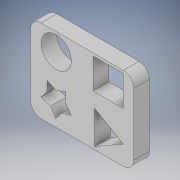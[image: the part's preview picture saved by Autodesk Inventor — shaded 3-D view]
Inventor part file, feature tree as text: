
AUTODESK INVENTOR PART (.ipt)
format: ipt  version: 2017 (Build 210142000, 142)  size: 197,120 bytes
history: native  units: in
note: dims shown in document units (in); Inventor stores cm internally (conversion verified against a paired STEP export)
features: extrude x2, shell x1, sketch x1, projected_geometry x1
ambient origin geometry x8: Origin, YZ Plane, XZ Plane, XY Plane, X Axis, Y Axis, Z Axis, Center Point
bodies: Solid1 (feature_tree)
feature tree (5):
  extrude  "Extrusion1"  Depth=1.59in
  extrude  "Extrusion2"  Depth=0.2in
  shell  "Shell1"  Thickness=0.3in
  sketch  "Sketch1"  dims[d0=1.975in d1=1.59in d2=0.2in d3=0.3in d4=0.0in d10=0.58in d11=0.05in d12=0.2in d13=0.58in d14=0.58in d15=0.58in d16=0.2in d17=0.05in d18=0.638in d19=0.2in d20=0.05in d21=0.605in d23=0.187in d25=0.187in d26=0.187in d27=0.187in d28=0.187in d29=0.187in d30=0.187in d31=0.187in d32=0.1869in d33=0.1541in d34=0.3in d35=0.0in d36=0.01in]
  projected_geometry  "Projected Loop1"
